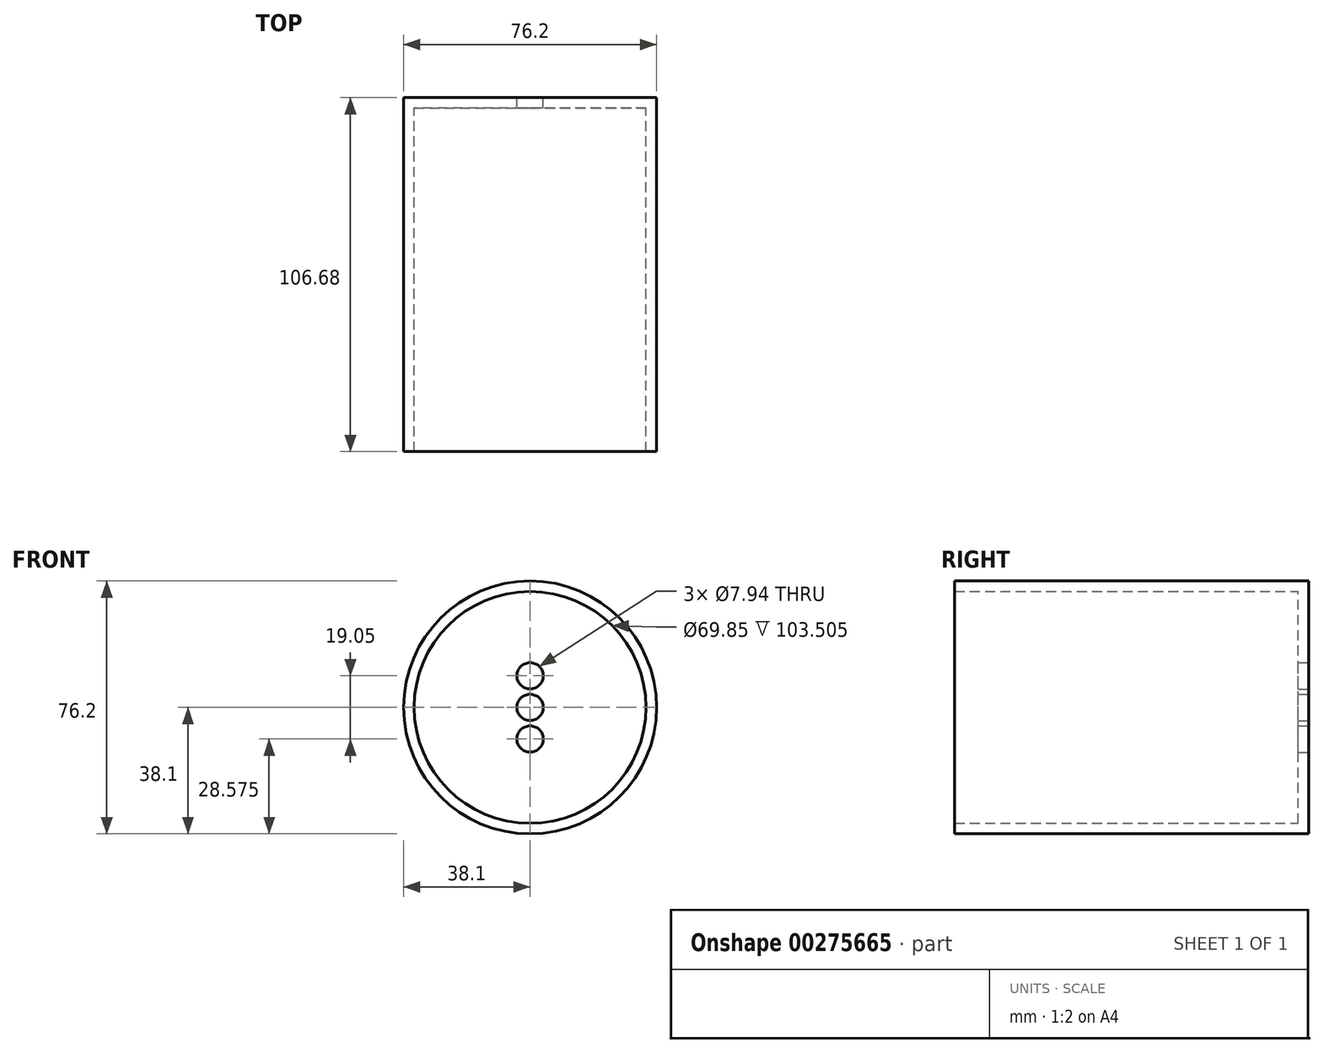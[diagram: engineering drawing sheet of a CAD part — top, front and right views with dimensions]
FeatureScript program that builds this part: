
annotation { "Feature Type Name" : "Feature", "Feature Type Description" : "" }
export const myFeature = defineFeature(function(context is Context, id is Id, definition is map)
    precondition{}
    {
        {
            var Q0;
            Q0=qCreatedBy(makeId("Front.planeOp"),FACE);
            var sketch = newSketch(context, id + "F0", { "sketchPlane" : qUnion([Q0])});
            skCircle(sketch, "E0", {"center": v(0, 0) * mm, "radius": 38.1 * mm});
            skCircle(sketch, "E1", {"center": v(0, 0) * mm, "radius": 34.93 * mm});
            skCircle(sketch, "E2", {"center": v(0, 0) * mm, "radius": 3.97 * mm});
            skLineSegment(sketch, "E3", {"start": v(-44.28, 0) * mm, "end": v(55.89, 0) * mm, "construction": true});
            skLineSegment(sketch, "E4", {"start": v(-10.25, -9.53) * mm, "end": v(13, -9.53) * mm, "construction": true});
            skLineSegment(sketch, "E5", {"start": v(-10.25, 9.53) * mm, "end": v(13.27, 9.53) * mm, "construction": true});
            skCircle(sketch, "E6", {"center": v(0, -9.53) * mm, "radius": 3.97 * mm});
            skPoint(sketch, "E6.centerSnap0", {"position": v(1.38, -9.53) * mm});
            skCircle(sketch, "E7", {"center": v(0, 9.53) * mm, "radius": 3.97 * mm});
            skPoint(sketch, "E7.centerSnap0", {"position": v(1.51, 9.53) * mm});
            skSolve(sketch);
        }
        {
            var Q0;
            Q0 = qSketchRegion(id + "F0", true);
            extrude(context, id + "F1", {"entities" : qUnion([Q0]), "depth" : 106.68 * mm});
        }
        {
            var Q0;
            Q0=makeQuery(id+"F0.imprint","IMPRINT",FACE,{"disambiguationData":[TD([[makeQuery(id+"F0.imprint","IMPRINT",EDGE,{"derivedFrom":sQuery(id+"F0.wireOp",EDGE,"E2")}),-1.0]])]});
            extrude(context, id + "F2", {"entities" : qUnion([Q0]), "operationType" : NewBodyOperationType.ADD, "depth" : 3.17 * mm});
        }
    });
